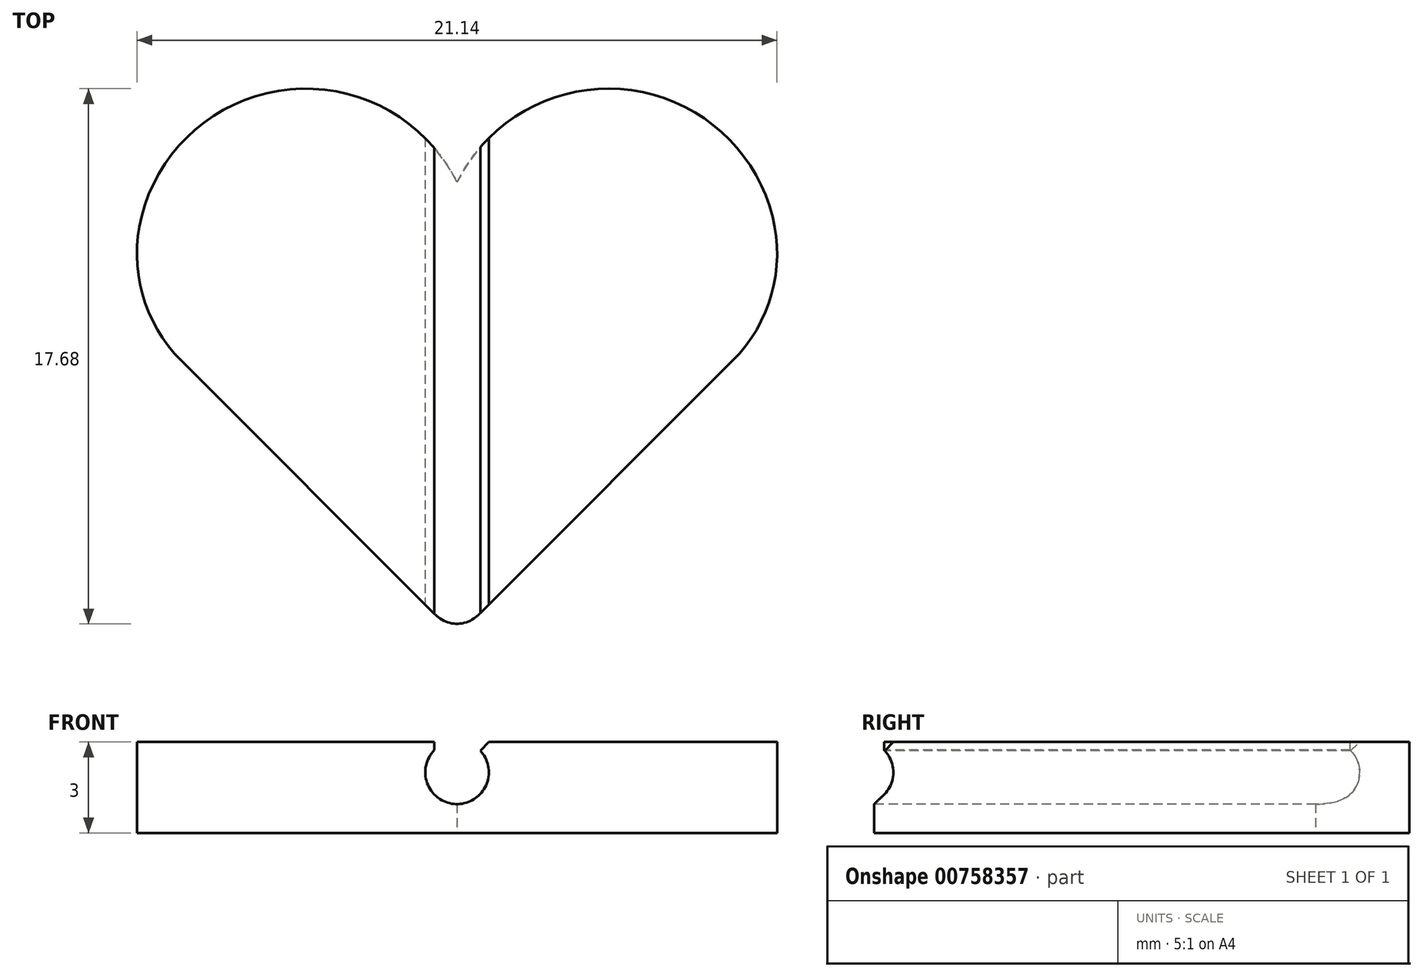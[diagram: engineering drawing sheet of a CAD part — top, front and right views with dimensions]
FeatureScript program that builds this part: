
annotation { "Feature Type Name" : "Feature", "Feature Type Description" : "" }
export const myFeature = defineFeature(function(context is Context, id is Id, definition is map)
    precondition{}
    {
        {
            var Q0;
            Q0=qCreatedBy(makeId("Top.planeOp"),FACE);
            var sketch = newSketch(context, id + "F0", { "sketchPlane" : qUnion([Q0])});
            skCircle(sketch, "E0.cCircle", {"center": v(0, 0) * mm, "radius": 10 * mm, "construction": true});
            skLineSegment(sketch, "E1", {"start": v(0, 0) * mm, "end": v(0, 10) * mm, "construction": true});
            skLineSegment(sketch, "E2", {"start": v(0, 0) * mm, "end": v(-10, 0) * mm, "construction": true});
            skLineSegment(sketch, "E3", {"start": v(-10, 0) * mm, "end": v(-10, 5) * mm, "construction": true});
            skPoint(sketch, "E3.endSnap0", {"position": v(0, 5) * mm});
            skLineSegment(sketch, "E4", {"start": v(-10, 2.5) * mm, "end": v(0, 2.5) * mm, "construction": true});
            skArc(sketch, "E5", {"start": v(0, 5) * mm, "mid": v(-7.5, 7.5) * mm, "end": v(-10, 0) * mm});
            skArc(sketch, "E6.MirrorC", {"start": v(0, 5) * mm, "mid": v(7.5, 7.5) * mm, "end": v(10, 0) * mm});
            skLineSegment(sketch, "E7", {"start": v(-10, 0) * mm, "end": v(0, -10) * mm});
            skLineSegment(sketch, "E8", {"start": v(0, -10) * mm, "end": v(10, 0) * mm});
            skSolve(sketch);
        }
        {
            var Q0;
            Q0=qSketchRegion(id+"F0",true);
            extrude(context, id + "F1", {"entities" : qUnion([Q0]), "depth" : 3 * mm, "offsetDistance" : 25 * mm});
        }
        {
            var Q0;
            Q0=makeQuery(id+"F1.opExtrude","CAP_FACE",FACE,{"disambiguationData":[OSD([sQuery(id+"F0.wireOp",EDGE,"E5"),sQuery(id+"F0.wireOp",EDGE,"E6.MirrorC"),sQuery(id+"F0.wireOp",EDGE,"E7"),sQuery(id+"F0.wireOp",EDGE,"E8")])],"isStart":false});
            var sketch = newSketch(context, id + "F2", { "sketchPlane" : qUnion([Q0])});
            skLineSegment(sketch, "E9.bottom", {"start": v(-2, 3.1) * mm, "end": v(2, 3.1) * mm});
            skLineSegment(sketch, "E9.top", {"start": v(-2, -3.1) * mm, "end": v(2, -3.1) * mm});
            skLineSegment(sketch, "E9.left", {"start": v(-2, 3.1) * mm, "end": v(-2, -3.1) * mm});
            skLineSegment(sketch, "E9.right", {"start": v(2, 3.1) * mm, "end": v(2, -3.1) * mm});
            skPoint(sketch, "E9.middle", {"position": v(0, 0) * mm});
            skSolve(sketch);
        }
        {
            var Q0;
            Q0=makeQuery(id+"F2.imprint","IMPRINT",FACE,{"disambiguationData":[TD([[makeQuery(id+"F2.imprint","IMPRINT",EDGE,{"derivedFrom":sQuery(id+"F2.wireOp",EDGE,"E9.bottom")}),1.0]])]});
            var Q1;
            Q1=makeQuery(id+"F2.imprint","IMPRINT",FACE,{"disambiguationData":[TD([[makeQuery(id+"F2.imprint","IMPRINT",EDGE,{"derivedFrom":sQuery(id+"F2.wireOp",EDGE,"E9.bottom")}),-1.0]])]});
            extrude(context, id + "F3", {"entities" : qUnion([Q0, Q1]), "operationType" : NewBodyOperationType.ADD, "depth" : 1 * mm, "offsetDistance" : 25 * mm});
        }
        {
            var Q0;
            Q0=qCreatedBy(makeId("Front.planeOp"),FACE);
            var sketch = newSketch(context, id + "F4", { "sketchPlane" : qUnion([Q0])});
            skLineSegment(sketch, "E10", {"start": v(0, 0) * mm, "end": v(0, 4.54) * mm, "construction": true});
            skLineSegment(sketch, "E11.bottom", {"start": v(-0.75, 4) * mm, "end": v(0.75, 4) * mm});
            skLineSegment(sketch, "E11.left", {"start": v(-0.75, 4) * mm, "end": v(-0.75, 3.73) * mm});
            skLineSegment(sketch, "E11.right", {"start": v(0.75, 4) * mm, "end": v(0.75, 3.73) * mm});
            skPoint(sketch, "E11.middle", {"position": v(0, 3) * mm});
            skArc(sketch, "E12.trimOffspring", {"start": v(-0.75, 3.73) * mm, "mid": v(0, 1.95) * mm, "end": v(0.75, 3.73) * mm});
            skPoint(sketch, "E13.orphan", {"position": v(0.75, 2) * mm});
            skPoint(sketch, "E14.orphan", {"position": v(-0.75, 2) * mm});
            skSolve(sketch);
        }
        {
            var Q0;
            Q0=qSketchRegion(id+"F4",true);
            var Q1;
            Q1=makeQuery(id+"F3.opExtrude","SWEPT_FACE",FACE,{"disambiguationData":[OSD([sQuery(id+"F2.wireOp",EDGE,"E9.bottom")])]});
            extrude(context, id + "F5", {"entities" : qUnion([Q0]), "operationType" : NewBodyOperationType.REMOVE, "endBound" : BoundingType.THROUGH_ALL, "oppositeDirection" : true, "depth" : 25 * mm, "endBoundEntityFace" : qUnion([Q1]), "offsetDistance" : 25 * mm, "hasSecondDirection" : true, "secondDirectionBound" : SecondDirectionBoundingType.THROUGH_ALL, "secondDirectionOppositeDirection" : false, "secondDirectionDepth" : 25 * mm});
        }
        {
            var Q0;
            Q0=makeQuery(id+"F5.boolean.opBoolean","COPY",EDGE,{"derivedFrom":makeQuery(id+"F5.opExtrude","SWEPT_EDGE",EDGE,{"disambiguationData":[OSD([sQuery(id+"F4.wireOp",EDGE,"E11.bottom"),sQuery(id+"F4.wireOp",EDGE,"E11.right")])]})});
            var Q1;
            Q1=makeQuery(id+"F5.boolean.opBoolean","COPY",EDGE,{"derivedFrom":makeQuery(id+"F5.opExtrude","SWEPT_EDGE",EDGE,{"disambiguationData":[OSD([sQuery(id+"F4.wireOp",EDGE,"E11.bottom"),sQuery(id+"F4.wireOp",EDGE,"E11.left")])]})});
            chamfer(context, id + "F6", {"entities" : qUnion([Q0, Q1]), "width" : 0.3 * mm, "tangentPropagation" : true});
        }
        {
            var Q0;
            Q0=makeQuery(id+"F1.opExtrude","CAP_FACE",FACE,{"disambiguationData":[OSD([sQuery(id+"F0.wireOp",EDGE,"E5"),sQuery(id+"F0.wireOp",EDGE,"E6.MirrorC"),sQuery(id+"F0.wireOp",EDGE,"E7"),sQuery(id+"F0.wireOp",EDGE,"E8")])],"isStart":true});
            extrude(context, id + "F7", {"entities" : qUnion([Q0]), "operationType" : NewBodyOperationType.REMOVE, "oppositeDirection" : true, "depth" : 1 * mm, "offsetDistance" : 25 * mm});
        }
        {
            var Q0;
            Q0=makeQuery(id+"F1.opExtrude","SWEPT_EDGE",EDGE,{"disambiguationData":[OSD([sQuery(id+"F0.wireOp",EDGE,"E6.MirrorC"),sQuery(id+"F0.wireOp",EDGE,"E8")])]});
            var Q1;
            Q1=makeQuery(id+"F1.opExtrude","SWEPT_EDGE",EDGE,{"disambiguationData":[OSD([sQuery(id+"F0.wireOp",EDGE,"E5"),sQuery(id+"F0.wireOp",EDGE,"E7")])]});
            fillet(context, id + "F8", {"entities" : qUnion([Q0, Q1]), "tangentPropagation" : true, "radius" : 5 * mm, "defaultsChanged" : false, "vertexSettings" : [], "allowEdgeOverflow" : false});
        }
        {
            var Q0;
            Q0=makeQuery(id+"F1.opExtrude","SWEPT_EDGE",EDGE,{"disambiguationData":[OSD([sQuery(id+"F0.wireOp",EDGE,"E7"),sQuery(id+"F0.wireOp",EDGE,"E8")])]});
            fillet(context, id + "F9", {"entities" : qUnion([Q0]), "tangentPropagation" : true, "radius" : 1 * mm, "defaultsChanged" : false, "vertexSettings" : [], "allowEdgeOverflow" : false});
        }
    });
